# Revit family: Haiku
name_source: partatom
category: Furniture
revit_build: Autodesk Revit 2015 (Build: 20140606_1530(x64)
units: mm (PartAtom-declared; Revit-internal decimal feet)

## types (48) — shared parameters
Manufacturer = Isku Oy
Type Comments = Available as antimicrobial
URL = www.isku.fi

## per-type parameters (varying)
| type | Rectangle table legs | Round leg position | Round table legs | Table depth | Table height | Table top | Table width |
| Haiku 7310 - table cover O6 | No | 295 mm  [stored 0.967848 ft] | Yes | 600 mm | 730 mm  [stored 2.39501 ft] | Table covers : O6 | 600 mm |
| Haiku 7310 - table cover O9 | No | 445 mm  [stored 1.45997 ft] | Yes | 550 mm | 730 mm  [stored 2.39501 ft] | Table covers : O9 | 550 mm |
| Haiku 7310 - table cover A12 | Yes | 507 mm | No | 800 mm  [stored 2.62467 ft] | 730 mm  [stored 2.39501 ft] | Table covers : A12 | 1200 mm |
| Haiku 7310 - table cover A14 | Yes | 507 mm | No | 800 mm  [stored 2.62467 ft] | 730 mm  [stored 2.39501 ft] | Table covers : A14 | 1400 mm  [stored 4.59318 ft] |
| Haiku 7310 - table cover A16 | Yes | 507 mm | No | 800 mm  [stored 2.62467 ft] | 730 mm  [stored 2.39501 ft] | Table covers : A16 | 1600 mm  [stored 5.24934 ft] |
| Haiku 7310 - table cover B6 | Yes | 507 mm | No | 600 mm | 730 mm  [stored 2.39501 ft] | Table covers : B6 | 600 mm |
| Haiku 7310 - table cover B8 | Yes | 507 mm | No | 600 mm | 730 mm  [stored 2.39501 ft] | Table covers : B8 | 800 mm  [stored 2.62467 ft] |
| Haiku 7310 - table cover B12 | Yes | 507 mm | No | 600 mm | 730 mm  [stored 2.39501 ft] | Table covers : B12 | 1200 mm |
| Haiku 7310 - table cover B10 | Yes | 507 mm | No | 600 mm | 730 mm  [stored 2.39501 ft] | Table covers : B10 | 1000 mm  [stored 3.28084 ft] |
| Haiku 7310 - table cover B14 | Yes | 507 mm | No | 600 mm | 730 mm  [stored 2.39501 ft] | Table covers : B14 | 1400 mm  [stored 4.59318 ft] |
| Haiku 7310 - table cover A10 | Yes | 507 mm | No | 800 mm  [stored 2.62467 ft] | 730 mm  [stored 2.39501 ft] | Table covers : A10 | 1000 mm  [stored 3.28084 ft] |
| Haiku 7310 - table cover A8 | Yes | 507 mm | No | 800 mm  [stored 2.62467 ft] | 730 mm  [stored 2.39501 ft] | Table covers : A8 | 800 mm  [stored 2.62467 ft] |
| Haiku 7311 - table cover O6 | No | 295 mm  [stored 0.967848 ft] | Yes | 600 mm | 780 mm  [stored 2.55906 ft] | Table covers : O6 | 600 mm |
| Haiku 7312 - table cover O6 | No | 295 mm  [stored 0.967848 ft] | Yes | 600 mm | 520 mm  [stored 1.70604 ft] | Table covers : O6 | 600 mm |
| Haiku 7313 - table cover O6 | No | 295 mm  [stored 0.967848 ft] | Yes | 600 mm | 650 mm  [stored 2.13255 ft] | Table covers : O6 | 600 mm |
| Haiku 7311 - table cover B8 | Yes | 507 mm | No | 600 mm | 780 mm  [stored 2.55906 ft] | Table covers : B8 | 800 mm  [stored 2.62467 ft] |
| Haiku 7312 - table cover B8 | Yes | 507 mm | No | 600 mm | 520 mm  [stored 1.70604 ft] | Table covers : B8 | 800 mm  [stored 2.62467 ft] |
| Haiku 7313 - table cover B8 | Yes | 507 mm | No | 600 mm | 650 mm  [stored 2.13255 ft] | Table covers : B8 | 800 mm  [stored 2.62467 ft] |
| Haiku 7311 - table cover B6 | Yes | 507 mm | No | 600 mm | 780 mm  [stored 2.55906 ft] | Table covers : B6 | 600 mm |
| Haiku 7312 - table cover B6 | Yes | 507 mm | No | 600 mm | 520 mm  [stored 1.70604 ft] | Table covers : B6 | 600 mm |
| Haiku 7313 - table cover B6 | Yes | 507 mm | No | 600 mm | 650 mm  [stored 2.13255 ft] | Table covers : B6 | 600 mm |
| Haiku 7311 - table cover O9 | No | 445 mm  [stored 1.45997 ft] | Yes | 550 mm | 780 mm  [stored 2.55906 ft] | Table covers : O9 | 550 mm |
| Haiku 7312 - table cover O9 | No | 445 mm  [stored 1.45997 ft] | Yes | 550 mm | 520 mm  [stored 1.70604 ft] | Table covers : O9 | 550 mm |
| Haiku 7313 - table cover O9 | No | 445 mm  [stored 1.45997 ft] | Yes | 550 mm | 650 mm  [stored 2.13255 ft] | Table covers : O9 | 550 mm |
| Haiku 7311 - table cover A10 | Yes | 507 mm | No | 800 mm  [stored 2.62467 ft] | 780 mm  [stored 2.55906 ft] | Table covers : A10 | 1000 mm  [stored 3.28084 ft] |
| Haiku 7312 - table cover A10 | Yes | 507 mm | No | 800 mm  [stored 2.62467 ft] | 520 mm  [stored 1.70604 ft] | Table covers : A10 | 1000 mm  [stored 3.28084 ft] |
| Haiku 7313 - table cover A10 | Yes | 507 mm | No | 800 mm  [stored 2.62467 ft] | 650 mm  [stored 2.13255 ft] | Table covers : A10 | 1000 mm  [stored 3.28084 ft] |
| Haiku 7311 - table cover A12 | Yes | 507 mm | No | 800 mm  [stored 2.62467 ft] | 780 mm  [stored 2.55906 ft] | Table covers : A12 | 1200 mm |
| Haiku 7312 - table cover A12 | Yes | 507 mm | No | 800 mm  [stored 2.62467 ft] | 520 mm  [stored 1.70604 ft] | Table covers : A12 | 1200 mm |
| Haiku 7313 - table cover A12 | Yes | 507 mm | No | 800 mm  [stored 2.62467 ft] | 650 mm  [stored 2.13255 ft] | Table covers : A12 | 1200 mm |
| Haiku 7311 - table cover A14 | Yes | 507 mm | No | 800 mm  [stored 2.62467 ft] | 780 mm  [stored 2.55906 ft] | Table covers : A14 | 1400 mm  [stored 4.59318 ft] |
| Haiku 7312 - table cover A14 | Yes | 507 mm | No | 800 mm  [stored 2.62467 ft] | 520 mm  [stored 1.70604 ft] | Table covers : A14 | 1400 mm  [stored 4.59318 ft] |
| Haiku 7313 - table cover A14 | Yes | 507 mm | No | 800 mm  [stored 2.62467 ft] | 650 mm  [stored 2.13255 ft] | Table covers : A14 | 1400 mm  [stored 4.59318 ft] |
| Haiku 7311 - table cover A16 | Yes | 507 mm | No | 800 mm  [stored 2.62467 ft] | 780 mm  [stored 2.55906 ft] | Table covers : A16 | 1600 mm  [stored 5.24934 ft] |
| Haiku 7312 - table cover A16 | Yes | 507 mm | No | 800 mm  [stored 2.62467 ft] | 520 mm  [stored 1.70604 ft] | Table covers : A16 | 1600 mm  [stored 5.24934 ft] |
| Haiku 7313 - table cover A16 | Yes | 507 mm | No | 800 mm  [stored 2.62467 ft] | 650 mm  [stored 2.13255 ft] | Table covers : A16 | 1600 mm  [stored 5.24934 ft] |
| Haiku 7311 - table cover B10 | Yes | 507 mm | No | 600 mm | 780 mm  [stored 2.55906 ft] | Table covers : B10 | 1000 mm  [stored 3.28084 ft] |
| Haiku 7312 - table cover B10 | Yes | 507 mm | No | 600 mm | 520 mm  [stored 1.70604 ft] | Table covers : B10 | 1000 mm  [stored 3.28084 ft] |
| Haiku 7313 - table cover B10 | Yes | 507 mm | No | 600 mm | 650 mm  [stored 2.13255 ft] | Table covers : B10 | 1000 mm  [stored 3.28084 ft] |
| Haiku 7311 - table cover A8 | Yes | 507 mm | No | 800 mm  [stored 2.62467 ft] | 780 mm  [stored 2.55906 ft] | Table covers : A8 | 800 mm  [stored 2.62467 ft] |
| Haiku 7312 - table cover A8 | Yes | 507 mm | No | 800 mm  [stored 2.62467 ft] | 520 mm  [stored 1.70604 ft] | Table covers : A8 | 800 mm  [stored 2.62467 ft] |
| Haiku 7313 - table cover A8 | Yes | 507 mm | No | 800 mm  [stored 2.62467 ft] | 650 mm  [stored 2.13255 ft] | Table covers : A8 | 800 mm  [stored 2.62467 ft] |
| Haiku 7311 - table cover B12 | Yes | 507 mm | No | 600 mm | 780 mm  [stored 2.55906 ft] | Table covers : B12 | 1200 mm |
| Haiku 7312 - table cover B12 | Yes | 507 mm | No | 600 mm | 520 mm  [stored 1.70604 ft] | Table covers : B12 | 1200 mm |
| Haiku 7313 - table cover B12 | Yes | 507 mm | No | 600 mm | 650 mm  [stored 2.13255 ft] | Table covers : B12 | 1200 mm |
| Haiku 7311 - table cover B14 | Yes | 507 mm | No | 600 mm | 780 mm  [stored 2.55906 ft] | Table covers : B14 | 1400 mm  [stored 4.59318 ft] |
| Haiku 7312 - table cover B14 | Yes | 507 mm | No | 600 mm | 520 mm  [stored 1.70604 ft] | Table covers : B14 | 1400 mm  [stored 4.59318 ft] |
| Haiku 7313 - table cover B14 | Yes | 507 mm | No | 600 mm | 650 mm  [stored 2.13255 ft] | Table covers : B14 | 1400 mm  [stored 4.59318 ft] |

note: [stored X ft] marks values corroborated as IEEE doubles in the binary element streams (Revit-internal decimal feet)

## geometry (parser evidence)
native form markers: Sweep x11
no freeform markers — native parametric forms only
